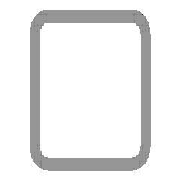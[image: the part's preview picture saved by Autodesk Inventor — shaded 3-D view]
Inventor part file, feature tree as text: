
AUTODESK INVENTOR PART (.ipt)
format: ipt  version: 2021 (Build 250183000, 183)  size: 140,288 bytes
history: native  units: mm (DEFAULTED — no unit token found)
features: other x5, sketch x3, extrude x1, split x1, plane x1
ambient origin geometry x8: Origin, YZ Plane, XZ Plane, XY Plane, X Axis, Y Axis, Z Axis, Center Point
bodies: Solid1 (feature_tree)
feature tree (11):
  parser-record x1  (decoder bookkeeping rows leaked as tree rows — omitted from the tree; the rows remain in map.json)
  other  "Driven Length"
  other  "Plano inicial"
  other  "Plano final"
  extrude  "Corpo"  TaperAngle=0.0deg  [1 undecoded]
  other  "Plano de trabalho4"
  split  "Dividir1"
  sketch  "Esboço"  dims[d11=50.8mm d12=4.7625mm d13=-0.0mm d14=1034.077676mm d15=25.4mm d16=25.4mm d17=9.525mm d18=90.0deg d19=1034.077676mm]
  sketch  "Sketch3"  dims[d3=1030.799585mm d4=0.0mm]
  plane  "Work Plane3"
  sketch  "Sketch4"  dims[d10=50.8mm]
note: 1 required parameter value undecoded (feature->parameter linkage not recoverable at this tier; creation-order binding heuristic only, values carry confidence <= 0.55)
